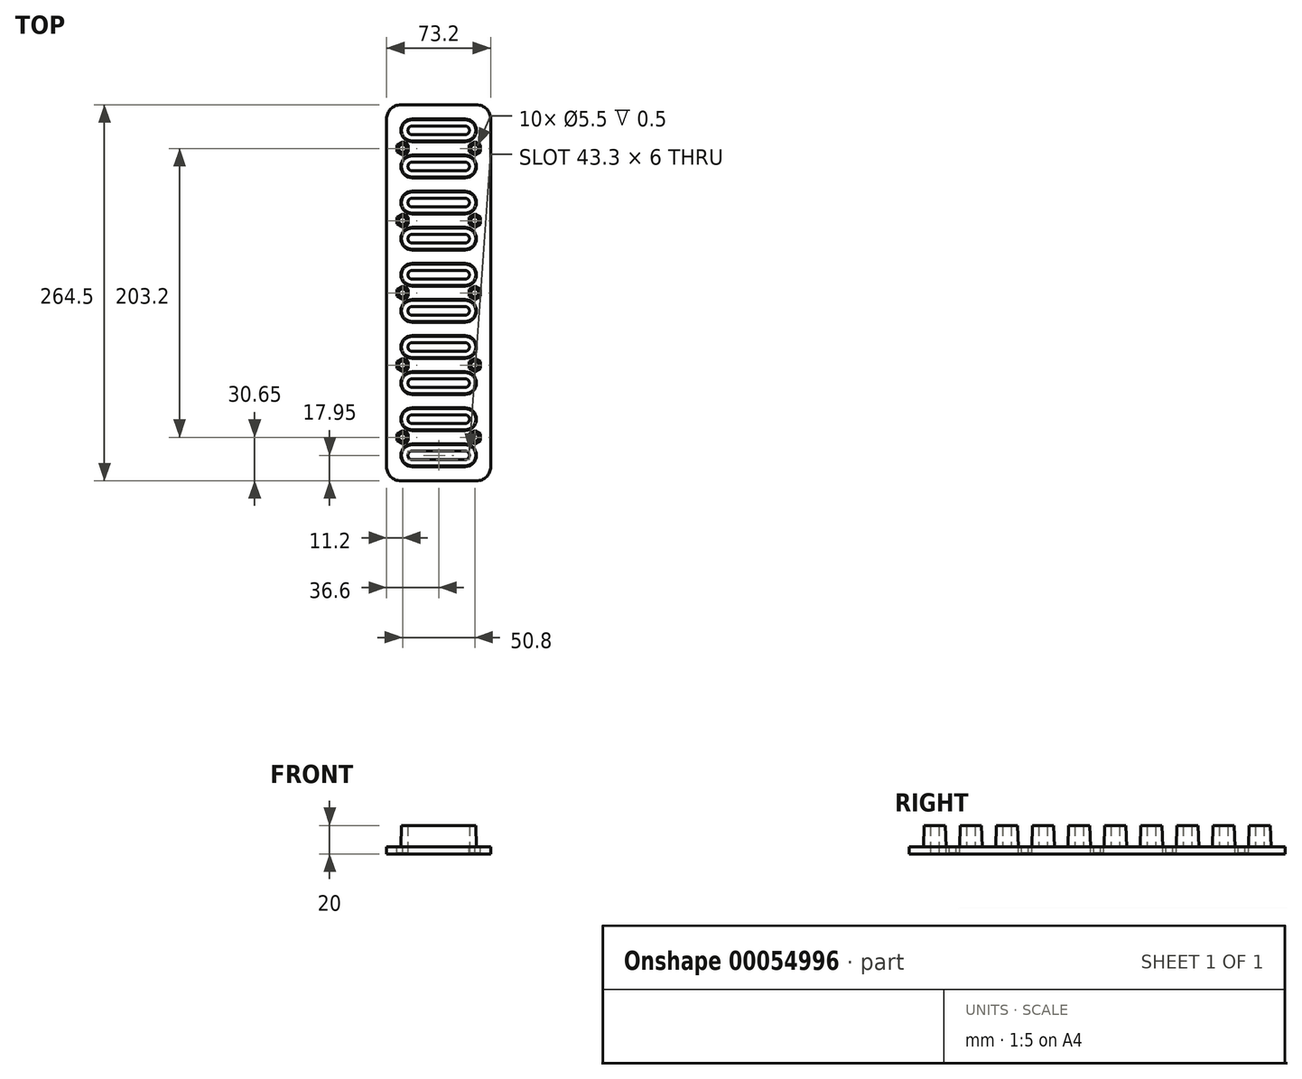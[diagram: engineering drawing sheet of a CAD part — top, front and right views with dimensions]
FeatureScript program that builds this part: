
annotation { "Feature Type Name" : "Feature", "Feature Type Description" : "" }
export const myFeature = defineFeature(function(context is Context, id is Id, definition is map)
    precondition{}
    {
        {
            var Q0;
            Q0=qCreatedBy(makeId("Top.planeOp"),FACE);
            var sketch = newSketch(context, id + "F0", { "sketchPlane" : qUnion([Q0])});
            skLineSegment(sketch, "E0.bottom", {"start": v(-18.65, 7.7) * mm, "end": v(18.65, 7.7) * mm});
            skLineSegment(sketch, "E0.top", {"start": v(-18.65, -7.7) * mm, "end": v(18.65, -7.7) * mm});
            skLineSegment(sketch, "E0.left", {"start": v(-26.35, 0) * mm, "end": v(-26.35, 0) * mm});
            skLineSegment(sketch, "E0.right", {"start": v(26.35, 0) * mm, "end": v(26.35, 0) * mm});
            skPoint(sketch, "E1", {"position": v(0, 7.7) * mm});
            skPoint(sketch, "E2", {"position": v(26.35, 0) * mm});
            skPoint(sketch, "E3.visualSharp", {"position": v(-26.35, 7.7) * mm});
            skArc(sketch, "E3.filletArc", {"start": v(-18.65, 7.7) * mm, "mid": v(-24.1, 5.44) * mm, "end": v(-26.35, 0) * mm});
            skPoint(sketch, "E4.visualSharp", {"position": v(-26.35, -7.7) * mm});
            skArc(sketch, "E4.filletArc", {"start": v(-26.35, 0) * mm, "mid": v(-24.1, -5.44) * mm, "end": v(-18.65, -7.7) * mm});
            skPoint(sketch, "E5.visualSharp", {"position": v(26.35, -7.7) * mm});
            skArc(sketch, "E5.filletArc", {"start": v(18.65, -7.7) * mm, "mid": v(24.1, -5.44) * mm, "end": v(26.35, 0) * mm});
            skPoint(sketch, "E6.visualSharp", {"position": v(26.35, 7.7) * mm});
            skArc(sketch, "E6.filletArc", {"start": v(26.35, 0) * mm, "mid": v(24.1, 5.44) * mm, "end": v(18.65, 7.7) * mm});
            skPoint(sketch, "E7.visualSharp", {"position": v(26.35, 33.1) * mm});
            skLineSegment(sketch, "E8.left", {"start": v(-26.35, 25.4) * mm, "end": v(-26.35, 25.4) * mm});
            skLineSegment(sketch, "E8.right", {"start": v(26.35, 25.4) * mm, "end": v(26.35, 25.4) * mm});
            skPoint(sketch, "E9.visualSharp", {"position": v(-26.35, 33.1) * mm});
            skLineSegment(sketch, "E8.bottom", {"start": v(-18.65, 33.1) * mm, "end": v(18.65, 33.1) * mm});
            skLineSegment(sketch, "E8.top", {"start": v(-18.65, 17.7) * mm, "end": v(18.65, 17.7) * mm});
            skArc(sketch, "E9.filletArc", {"start": v(-18.65, 33.1) * mm, "mid": v(-24.1, 30.84) * mm, "end": v(-26.35, 25.4) * mm});
            skArc(sketch, "E10.filletArc", {"start": v(-26.35, 25.4) * mm, "mid": v(-24.1, 19.96) * mm, "end": v(-18.65, 17.7) * mm});
            skArc(sketch, "E11.filletArc", {"start": v(18.65, 17.7) * mm, "mid": v(24.1, 19.96) * mm, "end": v(26.35, 25.4) * mm});
            skArc(sketch, "E7.filletArc", {"start": v(26.35, 25.4) * mm, "mid": v(24.1, 30.84) * mm, "end": v(18.65, 33.1) * mm});
            skPoint(sketch, "E10.visualSharp", {"position": v(-26.35, 17.7) * mm});
            skPoint(sketch, "E12", {"position": v(0, 33.1) * mm});
            skPoint(sketch, "E11.visualSharp", {"position": v(26.35, 17.7) * mm});
            skPoint(sketch, "E13", {"position": v(26.35, 25.4) * mm});
            skLineSegment(sketch, "E14", {"start": v(-26.35, -7.7) * mm, "end": v(-26.35, 17.7) * mm, "construction": true});
            skLineSegment(sketch, "E15.right", {"start": v(26.35, 50.8) * mm, "end": v(26.35, 50.8) * mm});
            skArc(sketch, "E16.filletArc", {"start": v(26.35, 76.2) * mm, "mid": v(24.1, 81.64) * mm, "end": v(18.65, 83.9) * mm});
            skPoint(sketch, "E17.visualSharp", {"position": v(26.35, 68.5) * mm});
            skPoint(sketch, "E18.visualSharp", {"position": v(-26.35, 58.5) * mm});
            skPoint(sketch, "E19.visualSharp", {"position": v(26.35, 58.5) * mm});
            skArc(sketch, "E20.filletArc", {"start": v(18.65, 43.1) * mm, "mid": v(24.1, 45.36) * mm, "end": v(26.35, 50.8) * mm});
            skArc(sketch, "E21.filletArc", {"start": v(-26.35, 50.8) * mm, "mid": v(-24.1, 45.36) * mm, "end": v(-18.65, 43.1) * mm});
            skLineSegment(sketch, "E15.top", {"start": v(-18.65, 43.1) * mm, "end": v(18.65, 43.1) * mm});
            skLineSegment(sketch, "E22.right", {"start": v(26.35, 76.2) * mm, "end": v(26.35, 76.2) * mm});
            skPoint(sketch, "E21.visualSharp", {"position": v(-26.35, 43.1) * mm});
            skLineSegment(sketch, "E15.left", {"start": v(-26.35, 50.8) * mm, "end": v(-26.35, 50.8) * mm});
            skPoint(sketch, "E16.visualSharp", {"position": v(26.35, 83.9) * mm});
            skPoint(sketch, "E23.visualSharp", {"position": v(-26.35, 83.9) * mm});
            skPoint(sketch, "E24.visualSharp", {"position": v(-26.35, 68.5) * mm});
            skPoint(sketch, "E25", {"position": v(0, 58.5) * mm});
            skPoint(sketch, "E26", {"position": v(0, 83.9) * mm});
            skLineSegment(sketch, "E15.bottom", {"start": v(-18.65, 58.5) * mm, "end": v(18.65, 58.5) * mm});
            skArc(sketch, "E18.filletArc", {"start": v(-18.65, 58.5) * mm, "mid": v(-24.1, 56.24) * mm, "end": v(-26.35, 50.8) * mm});
            skArc(sketch, "E19.filletArc", {"start": v(26.35, 50.8) * mm, "mid": v(24.1, 56.24) * mm, "end": v(18.65, 58.5) * mm});
            skLineSegment(sketch, "E22.left", {"start": v(-26.35, 76.2) * mm, "end": v(-26.35, 76.2) * mm});
            skPoint(sketch, "E20.visualSharp", {"position": v(26.35, 43.1) * mm});
            skLineSegment(sketch, "E22.bottom", {"start": v(-18.65, 83.9) * mm, "end": v(18.65, 83.9) * mm});
            skLineSegment(sketch, "E22.top", {"start": v(-18.65, 68.5) * mm, "end": v(18.65, 68.5) * mm});
            skArc(sketch, "E23.filletArc", {"start": v(-18.65, 83.9) * mm, "mid": v(-24.1, 81.64) * mm, "end": v(-26.35, 76.2) * mm});
            skArc(sketch, "E24.filletArc", {"start": v(-26.35, 76.2) * mm, "mid": v(-24.1, 70.76) * mm, "end": v(-18.65, 68.5) * mm});
            skArc(sketch, "E17.filletArc", {"start": v(18.65, 68.5) * mm, "mid": v(24.1, 70.76) * mm, "end": v(26.35, 76.2) * mm});
            skLineSegment(sketch, "E27", {"start": v(-26.35, 43.1) * mm, "end": v(-26.35, 68.5) * mm, "construction": true});
            skPoint(sketch, "E28", {"position": v(26.35, 76.2) * mm});
            skPoint(sketch, "E29", {"position": v(26.35, 50.8) * mm});
            skLineSegment(sketch, "E30", {"start": v(-26.35, 17.7) * mm, "end": v(-26.35, 43.1) * mm, "construction": true});
            skLineSegment(sketch, "E31.top", {"start": v(-18.65, 119.3) * mm, "end": v(18.65, 119.3) * mm});
            skArc(sketch, "E32.filletArc", {"start": v(-18.65, 109.3) * mm, "mid": v(-24.1, 107.04) * mm, "end": v(-26.35, 101.6) * mm});
            skPoint(sketch, "E33.visualSharp", {"position": v(26.35, 119.3) * mm});
            skPoint(sketch, "E32.visualSharp", {"position": v(-26.35, 109.3) * mm});
            skLineSegment(sketch, "E31.right", {"start": v(26.35, 127) * mm, "end": v(26.35, 127) * mm});
            skLineSegment(sketch, "E34", {"start": v(-26.35, 144.7) * mm, "end": v(-26.35, 170.1) * mm, "construction": true});
            skPoint(sketch, "E35.visualSharp", {"position": v(-26.35, 144.7) * mm});
            skArc(sketch, "E36.filletArc", {"start": v(-26.35, 177.8) * mm, "mid": v(-24.1, 172.36) * mm, "end": v(-18.65, 170.1) * mm});
            skLineSegment(sketch, "E37.right", {"start": v(26.35, 177.8) * mm, "end": v(26.35, 177.8) * mm});
            skLineSegment(sketch, "E31.left", {"start": v(-26.35, 127) * mm, "end": v(-26.35, 127) * mm});
            skLineSegment(sketch, "E38", {"start": v(-26.35, 93.9) * mm, "end": v(-26.35, 119.3) * mm, "construction": true});
            skArc(sketch, "E39.filletArc", {"start": v(26.35, 127) * mm, "mid": v(24.1, 132.44) * mm, "end": v(18.65, 134.7) * mm});
            skArc(sketch, "E33.filletArc", {"start": v(18.65, 119.3) * mm, "mid": v(24.1, 121.56) * mm, "end": v(26.35, 127) * mm});
            skPoint(sketch, "E40.visualSharp", {"position": v(26.35, 144.7) * mm});
            skArc(sketch, "E41.filletArc", {"start": v(-26.35, 127) * mm, "mid": v(-24.1, 121.56) * mm, "end": v(-18.65, 119.3) * mm});
            skArc(sketch, "E42.filletArc", {"start": v(-18.65, 134.7) * mm, "mid": v(-24.1, 132.44) * mm, "end": v(-26.35, 127) * mm});
            skPoint(sketch, "E42.visualSharp", {"position": v(-26.35, 134.7) * mm});
            skArc(sketch, "E43.filletArc", {"start": v(18.65, 170.1) * mm, "mid": v(24.1, 172.36) * mm, "end": v(26.35, 177.8) * mm});
            skPoint(sketch, "E44", {"position": v(0, 134.7) * mm});
            skLineSegment(sketch, "E45.right", {"start": v(26.35, 101.6) * mm, "end": v(26.35, 101.6) * mm});
            skPoint(sketch, "E36.visualSharp", {"position": v(-26.35, 170.1) * mm});
            skLineSegment(sketch, "E46", {"start": v(-26.35, 119.3) * mm, "end": v(-26.35, 144.7) * mm, "construction": true});
            skArc(sketch, "E40.filletArc", {"start": v(18.65, 144.7) * mm, "mid": v(24.1, 146.96) * mm, "end": v(26.35, 152.4) * mm});
            skLineSegment(sketch, "E47.left", {"start": v(-26.35, 152.4) * mm, "end": v(-26.35, 152.4) * mm});
            skArc(sketch, "E35.filletArc", {"start": v(-26.35, 152.4) * mm, "mid": v(-24.1, 146.96) * mm, "end": v(-18.65, 144.7) * mm});
            skLineSegment(sketch, "E45.bottom", {"start": v(-18.65, 109.3) * mm, "end": v(18.65, 109.3) * mm});
            skLineSegment(sketch, "E45.top", {"start": v(-18.65, 93.9) * mm, "end": v(18.65, 93.9) * mm});
            skArc(sketch, "E48.filletArc", {"start": v(18.65, 93.9) * mm, "mid": v(24.1, 96.16) * mm, "end": v(26.35, 101.6) * mm});
            skArc(sketch, "E49.filletArc", {"start": v(26.35, 101.6) * mm, "mid": v(24.1, 107.04) * mm, "end": v(18.65, 109.3) * mm});
            skLineSegment(sketch, "E37.left", {"start": v(-26.35, 177.8) * mm, "end": v(-26.35, 177.8) * mm});
            skPoint(sketch, "E43.visualSharp", {"position": v(26.35, 170.1) * mm});
            skLineSegment(sketch, "E37.bottom", {"start": v(-18.65, 185.5) * mm, "end": v(18.65, 185.5) * mm});
            skArc(sketch, "E50.filletArc", {"start": v(-26.35, 101.6) * mm, "mid": v(-24.1, 96.16) * mm, "end": v(-18.65, 93.9) * mm});
            skPoint(sketch, "E51", {"position": v(0, 160.1) * mm});
            skPoint(sketch, "E50.visualSharp", {"position": v(-26.35, 93.9) * mm});
            skArc(sketch, "E52.filletArc", {"start": v(26.35, 177.8) * mm, "mid": v(24.1, 183.24) * mm, "end": v(18.65, 185.5) * mm});
            skArc(sketch, "E53.filletArc", {"start": v(-18.65, 160.1) * mm, "mid": v(-24.1, 157.84) * mm, "end": v(-26.35, 152.4) * mm});
            skPoint(sketch, "E54.visualSharp", {"position": v(-26.35, 185.5) * mm});
            skLineSegment(sketch, "E47.right", {"start": v(26.35, 152.4) * mm, "end": v(26.35, 152.4) * mm});
            skLineSegment(sketch, "E47.bottom", {"start": v(-18.65, 160.1) * mm, "end": v(18.65, 160.1) * mm});
            skPoint(sketch, "E52.visualSharp", {"position": v(26.35, 185.5) * mm});
            skLineSegment(sketch, "E47.top", {"start": v(-18.65, 144.7) * mm, "end": v(18.65, 144.7) * mm});
            skArc(sketch, "E54.filletArc", {"start": v(-18.65, 185.5) * mm, "mid": v(-24.1, 183.24) * mm, "end": v(-26.35, 177.8) * mm});
            skPoint(sketch, "E55", {"position": v(0, 109.3) * mm});
            skLineSegment(sketch, "E37.top", {"start": v(-18.65, 170.1) * mm, "end": v(18.65, 170.1) * mm});
            skPoint(sketch, "E41.visualSharp", {"position": v(-26.35, 119.3) * mm});
            skPoint(sketch, "E56", {"position": v(0, 185.5) * mm});
            skLineSegment(sketch, "E45.left", {"start": v(-26.35, 101.6) * mm, "end": v(-26.35, 101.6) * mm});
            skPoint(sketch, "E49.visualSharp", {"position": v(26.35, 109.3) * mm});
            skPoint(sketch, "E57.visualSharp", {"position": v(26.35, 160.1) * mm});
            skLineSegment(sketch, "E31.bottom", {"start": v(-18.65, 134.7) * mm, "end": v(18.65, 134.7) * mm});
            skArc(sketch, "E57.filletArc", {"start": v(26.35, 152.4) * mm, "mid": v(24.1, 157.84) * mm, "end": v(18.65, 160.1) * mm});
            skPoint(sketch, "E39.visualSharp", {"position": v(26.35, 134.7) * mm});
            skPoint(sketch, "E48.visualSharp", {"position": v(26.35, 93.9) * mm});
            skPoint(sketch, "E53.visualSharp", {"position": v(-26.35, 160.1) * mm});
            skPoint(sketch, "E58", {"position": v(26.35, 152.4) * mm});
            skPoint(sketch, "E59", {"position": v(26.35, 127) * mm});
            skPoint(sketch, "E60", {"position": v(26.35, 101.6) * mm});
            skPoint(sketch, "E61", {"position": v(26.35, 177.8) * mm});
            skLineSegment(sketch, "E62", {"start": v(-26.35, 68.5) * mm, "end": v(-26.35, 93.9) * mm, "construction": true});
            skLineSegment(sketch, "E63", {"start": v(-26.35, 195.5) * mm, "end": v(-26.35, 220.9) * mm, "construction": true});
            skLineSegment(sketch, "E64.left", {"start": v(-26.35, 228.6) * mm, "end": v(-26.35, 228.6) * mm});
            skLineSegment(sketch, "E64.top", {"start": v(-18.65, 220.9) * mm, "end": v(18.65, 220.9) * mm});
            skPoint(sketch, "E65.visualSharp", {"position": v(26.35, 220.9) * mm});
            skArc(sketch, "E66.filletArc", {"start": v(-18.65, 210.9) * mm, "mid": v(-24.1, 208.64) * mm, "end": v(-26.35, 203.2) * mm});
            skPoint(sketch, "E67.visualSharp", {"position": v(-26.35, 195.5) * mm});
            skArc(sketch, "E68.filletArc", {"start": v(-18.65, 236.3) * mm, "mid": v(-24.1, 234.04) * mm, "end": v(-26.35, 228.6) * mm});
            skLineSegment(sketch, "E69", {"start": v(-26.35, 170.1) * mm, "end": v(-26.35, 195.5) * mm, "construction": true});
            skLineSegment(sketch, "E70.bottom", {"start": v(-18.65, 210.9) * mm, "end": v(18.65, 210.9) * mm});
            skPoint(sketch, "E71.visualSharp", {"position": v(26.35, 195.5) * mm});
            skLineSegment(sketch, "E70.left", {"start": v(-26.35, 203.2) * mm, "end": v(-26.35, 203.2) * mm});
            skLineSegment(sketch, "E64.bottom", {"start": v(-18.65, 236.3) * mm, "end": v(18.65, 236.3) * mm});
            skArc(sketch, "E72.filletArc", {"start": v(26.35, 203.2) * mm, "mid": v(24.1, 208.64) * mm, "end": v(18.65, 210.9) * mm});
            skArc(sketch, "E73.filletArc", {"start": v(26.35, 228.6) * mm, "mid": v(24.1, 234.04) * mm, "end": v(18.65, 236.3) * mm});
            skPoint(sketch, "E74.visualSharp", {"position": v(-26.35, 220.9) * mm});
            skArc(sketch, "E74.filletArc", {"start": v(-26.35, 228.6) * mm, "mid": v(-24.1, 223.16) * mm, "end": v(-18.65, 220.9) * mm});
            skPoint(sketch, "E66.visualSharp", {"position": v(-26.35, 210.9) * mm});
            skArc(sketch, "E65.filletArc", {"start": v(18.65, 220.9) * mm, "mid": v(24.1, 223.16) * mm, "end": v(26.35, 228.6) * mm});
            skPoint(sketch, "E72.visualSharp", {"position": v(26.35, 210.9) * mm});
            skPoint(sketch, "E75", {"position": v(0, 236.3) * mm});
            skPoint(sketch, "E68.visualSharp", {"position": v(-26.35, 236.3) * mm});
            skArc(sketch, "E67.filletArc", {"start": v(-26.35, 203.2) * mm, "mid": v(-24.1, 197.76) * mm, "end": v(-18.65, 195.5) * mm});
            skLineSegment(sketch, "E70.right", {"start": v(26.35, 203.2) * mm, "end": v(26.35, 203.2) * mm});
            skLineSegment(sketch, "E70.top", {"start": v(-18.65, 195.5) * mm, "end": v(18.65, 195.5) * mm});
            skArc(sketch, "E71.filletArc", {"start": v(18.65, 195.5) * mm, "mid": v(24.1, 197.76) * mm, "end": v(26.35, 203.2) * mm});
            skPoint(sketch, "E76", {"position": v(0, 210.9) * mm});
            skPoint(sketch, "E73.visualSharp", {"position": v(26.35, 236.3) * mm});
            skLineSegment(sketch, "E64.right", {"start": v(26.35, 228.6) * mm, "end": v(26.35, 228.6) * mm});
            skPoint(sketch, "E77", {"position": v(26.35, 203.2) * mm});
            skPoint(sketch, "E78", {"position": v(26.35, 228.6) * mm});
            skSolve(sketch);
        }
        {
            var Q0;
            Q0=qCreatedBy(makeId("Top.planeOp"),FACE);
            var sketch = newSketch(context, id + "F1", { "sketchPlane" : qUnion([Q0])});
            skLineSegment(sketch, "E79.bottom", {"start": v(-18.65, 3) * mm, "end": v(18.65, 3) * mm});
            skLineSegment(sketch, "E79.top", {"start": v(-18.65, -3) * mm, "end": v(18.65, -3) * mm});
            skLineSegment(sketch, "E79.left", {"start": v(-21.65, 0) * mm, "end": v(-21.65, 0) * mm});
            skLineSegment(sketch, "E79.right", {"start": v(21.65, 0) * mm, "end": v(21.65, 0) * mm});
            skPoint(sketch, "E80", {"position": v(0, 3) * mm});
            skPoint(sketch, "E81", {"position": v(21.65, 0) * mm});
            skPoint(sketch, "E82.visualSharp", {"position": v(-21.65, 3) * mm});
            skArc(sketch, "E82.filletArc", {"start": v(-18.65, 3) * mm, "mid": v(-20.77, 2.12) * mm, "end": v(-21.65, 0) * mm});
            skPoint(sketch, "E83.visualSharp", {"position": v(-21.65, -3) * mm});
            skArc(sketch, "E83.filletArc", {"start": v(-21.65, 0) * mm, "mid": v(-20.77, -2.12) * mm, "end": v(-18.65, -3) * mm});
            skPoint(sketch, "E84.visualSharp", {"position": v(21.65, -3) * mm});
            skArc(sketch, "E84.filletArc", {"start": v(18.65, -3) * mm, "mid": v(20.77, -2.12) * mm, "end": v(21.65, 0) * mm});
            skPoint(sketch, "E85.visualSharp", {"position": v(21.65, 3) * mm});
            skArc(sketch, "E85.filletArc", {"start": v(21.65, 0) * mm, "mid": v(20.77, 2.12) * mm, "end": v(18.65, 3) * mm});
            skPoint(sketch, "E86.visualSharp", {"position": v(21.65, 28.4) * mm});
            skLineSegment(sketch, "E87.left", {"start": v(-21.65, 25.4) * mm, "end": v(-21.65, 25.4) * mm});
            skLineSegment(sketch, "E87.right", {"start": v(21.65, 25.4) * mm, "end": v(21.65, 25.4) * mm});
            skPoint(sketch, "E88.visualSharp", {"position": v(-21.65, 22.4) * mm});
            skPoint(sketch, "E89.visualSharp", {"position": v(-21.65, 28.4) * mm});
            skLineSegment(sketch, "E87.bottom", {"start": v(-18.65, 28.4) * mm, "end": v(18.65, 28.4) * mm});
            skLineSegment(sketch, "E87.top", {"start": v(-18.65, 22.4) * mm, "end": v(18.65, 22.4) * mm});
            skPoint(sketch, "E90", {"position": v(0, 28.4) * mm});
            skPoint(sketch, "E91.visualSharp", {"position": v(21.65, 22.4) * mm});
            skPoint(sketch, "E92", {"position": v(21.65, 25.4) * mm});
            skArc(sketch, "E89.filletArc", {"start": v(-18.65, 28.4) * mm, "mid": v(-20.77, 27.52) * mm, "end": v(-21.65, 25.4) * mm});
            skArc(sketch, "E88.filletArc", {"start": v(-21.65, 25.4) * mm, "mid": v(-20.77, 23.28) * mm, "end": v(-18.65, 22.4) * mm});
            skArc(sketch, "E91.filletArc", {"start": v(18.65, 22.4) * mm, "mid": v(20.77, 23.28) * mm, "end": v(21.65, 25.4) * mm});
            skArc(sketch, "E86.filletArc", {"start": v(21.65, 25.4) * mm, "mid": v(20.77, 27.52) * mm, "end": v(18.65, 28.4) * mm});
            skLineSegment(sketch, "E93", {"start": v(-21.65, 22.4) * mm, "end": v(-21.65, -3) * mm, "construction": true});
            skLineSegment(sketch, "E94.right", {"start": v(21.65, 76.2) * mm, "end": v(21.65, 76.2) * mm});
            skPoint(sketch, "E95.visualSharp", {"position": v(-21.65, 79.2) * mm});
            skPoint(sketch, "E96.visualSharp", {"position": v(21.65, 73.2) * mm});
            skLineSegment(sketch, "E94.left", {"start": v(-21.65, 76.2) * mm, "end": v(-21.65, 76.2) * mm});
            skLineSegment(sketch, "E94.top", {"start": v(-18.65, 73.2) * mm, "end": v(18.65, 73.2) * mm});
            skLineSegment(sketch, "E94.bottom", {"start": v(-18.65, 79.2) * mm, "end": v(18.65, 79.2) * mm});
            skLineSegment(sketch, "E97.right", {"start": v(21.65, 50.8) * mm, "end": v(21.65, 50.8) * mm});
            skPoint(sketch, "E98.visualSharp", {"position": v(-21.65, 53.8) * mm});
            skPoint(sketch, "E99.visualSharp", {"position": v(21.65, 47.8) * mm});
            skPoint(sketch, "E100", {"position": v(0, 53.8) * mm});
            skPoint(sketch, "E101", {"position": v(0, 79.2) * mm});
            skLineSegment(sketch, "E102", {"start": v(-21.65, 73.2) * mm, "end": v(-21.65, 47.8) * mm, "construction": true});
            skPoint(sketch, "E103.visualSharp", {"position": v(-21.65, 73.2) * mm});
            skPoint(sketch, "E104.visualSharp", {"position": v(-21.65, 47.8) * mm});
            skPoint(sketch, "E105.visualSharp", {"position": v(21.65, 79.2) * mm});
            skLineSegment(sketch, "E97.left", {"start": v(-21.65, 50.8) * mm, "end": v(-21.65, 50.8) * mm});
            skPoint(sketch, "E106.visualSharp", {"position": v(21.65, 53.8) * mm});
            skLineSegment(sketch, "E97.top", {"start": v(-18.65, 47.8) * mm, "end": v(18.65, 47.8) * mm});
            skLineSegment(sketch, "E97.bottom", {"start": v(-18.65, 53.8) * mm, "end": v(18.65, 53.8) * mm});
            skArc(sketch, "E105.filletArc", {"start": v(21.65, 76.2) * mm, "mid": v(20.77, 78.32) * mm, "end": v(18.65, 79.2) * mm});
            skArc(sketch, "E106.filletArc", {"start": v(21.65, 50.8) * mm, "mid": v(20.77, 52.92) * mm, "end": v(18.65, 53.8) * mm});
            skArc(sketch, "E99.filletArc", {"start": v(18.65, 47.8) * mm, "mid": v(20.77, 48.68) * mm, "end": v(21.65, 50.8) * mm});
            skArc(sketch, "E95.filletArc", {"start": v(-18.65, 79.2) * mm, "mid": v(-20.77, 78.32) * mm, "end": v(-21.65, 76.2) * mm});
            skPoint(sketch, "E107", {"position": v(21.65, 76.2) * mm});
            skArc(sketch, "E96.filletArc", {"start": v(18.65, 73.2) * mm, "mid": v(20.77, 74.08) * mm, "end": v(21.65, 76.2) * mm});
            skPoint(sketch, "E108", {"position": v(21.65, 50.8) * mm});
            skArc(sketch, "E98.filletArc", {"start": v(-18.65, 53.8) * mm, "mid": v(-20.77, 52.92) * mm, "end": v(-21.65, 50.8) * mm});
            skArc(sketch, "E103.filletArc", {"start": v(-21.65, 76.2) * mm, "mid": v(-20.77, 74.08) * mm, "end": v(-18.65, 73.2) * mm});
            skArc(sketch, "E104.filletArc", {"start": v(-21.65, 50.8) * mm, "mid": v(-20.77, 48.68) * mm, "end": v(-18.65, 47.8) * mm});
            skLineSegment(sketch, "E109", {"start": v(-21.65, 22.4) * mm, "end": v(-21.65, 47.8) * mm, "construction": true});
            skPoint(sketch, "E110.visualSharp", {"position": v(-21.65, 130) * mm});
            skPoint(sketch, "E111.visualSharp", {"position": v(21.65, 180.8) * mm});
            skLineSegment(sketch, "E112.right", {"start": v(21.65, 177.8) * mm, "end": v(21.65, 177.8) * mm});
            skPoint(sketch, "E113.visualSharp", {"position": v(-21.65, 155.4) * mm});
            skLineSegment(sketch, "E112.left", {"start": v(-21.65, 177.8) * mm, "end": v(-21.65, 177.8) * mm});
            skPoint(sketch, "E114.visualSharp", {"position": v(21.65, 155.4) * mm});
            skPoint(sketch, "E115", {"position": v(0, 130) * mm});
            skLineSegment(sketch, "E116", {"start": v(-21.65, 124) * mm, "end": v(-21.65, 149.4) * mm, "construction": true});
            skLineSegment(sketch, "E117.top", {"start": v(-18.65, 124) * mm, "end": v(18.65, 124) * mm});
            skPoint(sketch, "E118.visualSharp", {"position": v(-21.65, 98.6) * mm});
            skLineSegment(sketch, "E119.left", {"start": v(-21.65, 101.6) * mm, "end": v(-21.65, 101.6) * mm});
            skLineSegment(sketch, "E120.left", {"start": v(-21.65, 152.4) * mm, "end": v(-21.65, 152.4) * mm});
            skPoint(sketch, "E121.visualSharp", {"position": v(21.65, 149.4) * mm});
            skLineSegment(sketch, "E119.right", {"start": v(21.65, 101.6) * mm, "end": v(21.65, 101.6) * mm});
            skPoint(sketch, "E122.visualSharp", {"position": v(-21.65, 180.8) * mm});
            skPoint(sketch, "E123", {"position": v(0, 104.6) * mm});
            skLineSegment(sketch, "E117.left", {"start": v(-21.65, 127) * mm, "end": v(-21.65, 127) * mm});
            skPoint(sketch, "E124.visualSharp", {"position": v(-21.65, 174.8) * mm});
            skLineSegment(sketch, "E120.top", {"start": v(-18.65, 149.4) * mm, "end": v(18.65, 149.4) * mm});
            skPoint(sketch, "E125", {"position": v(0, 180.8) * mm});
            skLineSegment(sketch, "E120.right", {"start": v(21.65, 152.4) * mm, "end": v(21.65, 152.4) * mm});
            skPoint(sketch, "E126", {"position": v(0, 155.4) * mm});
            skPoint(sketch, "E127.visualSharp", {"position": v(21.65, 98.6) * mm});
            skPoint(sketch, "E128.visualSharp", {"position": v(21.65, 104.6) * mm});
            skPoint(sketch, "E129.visualSharp", {"position": v(21.65, 124) * mm});
            skPoint(sketch, "E130.visualSharp", {"position": v(-21.65, 104.6) * mm});
            skLineSegment(sketch, "E120.bottom", {"start": v(-18.65, 155.4) * mm, "end": v(18.65, 155.4) * mm});
            skLineSegment(sketch, "E131", {"start": v(-21.65, 124) * mm, "end": v(-21.65, 98.6) * mm, "construction": true});
            skLineSegment(sketch, "E117.bottom", {"start": v(-18.65, 130) * mm, "end": v(18.65, 130) * mm});
            skLineSegment(sketch, "E119.top", {"start": v(-18.65, 98.6) * mm, "end": v(18.65, 98.6) * mm});
            skLineSegment(sketch, "E119.bottom", {"start": v(-18.65, 104.6) * mm, "end": v(18.65, 104.6) * mm});
            skLineSegment(sketch, "E132", {"start": v(-21.65, 174.8) * mm, "end": v(-21.65, 149.4) * mm, "construction": true});
            skLineSegment(sketch, "E112.bottom", {"start": v(-18.65, 180.8) * mm, "end": v(18.65, 180.8) * mm});
            skLineSegment(sketch, "E112.top", {"start": v(-18.65, 174.8) * mm, "end": v(18.65, 174.8) * mm});
            skPoint(sketch, "E133.visualSharp", {"position": v(-21.65, 124) * mm});
            skPoint(sketch, "E134.visualSharp", {"position": v(-21.65, 149.4) * mm});
            skLineSegment(sketch, "E117.right", {"start": v(21.65, 127) * mm, "end": v(21.65, 127) * mm});
            skPoint(sketch, "E135.visualSharp", {"position": v(21.65, 174.8) * mm});
            skPoint(sketch, "E136.visualSharp", {"position": v(21.65, 130) * mm});
            skPoint(sketch, "E137", {"position": v(21.65, 177.8) * mm});
            skArc(sketch, "E136.filletArc", {"start": v(21.65, 127) * mm, "mid": v(20.77, 129.12) * mm, "end": v(18.65, 130) * mm});
            skArc(sketch, "E129.filletArc", {"start": v(18.65, 124) * mm, "mid": v(20.77, 124.88) * mm, "end": v(21.65, 127) * mm});
            skArc(sketch, "E114.filletArc", {"start": v(21.65, 152.4) * mm, "mid": v(20.77, 154.52) * mm, "end": v(18.65, 155.4) * mm});
            skArc(sketch, "E122.filletArc", {"start": v(-18.65, 180.8) * mm, "mid": v(-20.77, 179.92) * mm, "end": v(-21.65, 177.8) * mm});
            skArc(sketch, "E135.filletArc", {"start": v(18.65, 174.8) * mm, "mid": v(20.77, 175.68) * mm, "end": v(21.65, 177.8) * mm});
            skArc(sketch, "E111.filletArc", {"start": v(21.65, 177.8) * mm, "mid": v(20.77, 179.92) * mm, "end": v(18.65, 180.8) * mm});
            skPoint(sketch, "E138", {"position": v(21.65, 152.4) * mm});
            skArc(sketch, "E110.filletArc", {"start": v(-18.65, 130) * mm, "mid": v(-20.77, 129.12) * mm, "end": v(-21.65, 127) * mm});
            skPoint(sketch, "E139", {"position": v(21.65, 127) * mm});
            skPoint(sketch, "E140", {"position": v(21.65, 101.6) * mm});
            skArc(sketch, "E134.filletArc", {"start": v(-21.65, 152.4) * mm, "mid": v(-20.77, 150.28) * mm, "end": v(-18.65, 149.4) * mm});
            skArc(sketch, "E121.filletArc", {"start": v(18.65, 149.4) * mm, "mid": v(20.77, 150.28) * mm, "end": v(21.65, 152.4) * mm});
            skArc(sketch, "E127.filletArc", {"start": v(18.65, 98.6) * mm, "mid": v(20.77, 99.48) * mm, "end": v(21.65, 101.6) * mm});
            skArc(sketch, "E128.filletArc", {"start": v(21.65, 101.6) * mm, "mid": v(20.77, 103.72) * mm, "end": v(18.65, 104.6) * mm});
            skArc(sketch, "E130.filletArc", {"start": v(-18.65, 104.6) * mm, "mid": v(-20.77, 103.72) * mm, "end": v(-21.65, 101.6) * mm});
            skArc(sketch, "E113.filletArc", {"start": v(-18.65, 155.4) * mm, "mid": v(-20.77, 154.52) * mm, "end": v(-21.65, 152.4) * mm});
            skArc(sketch, "E133.filletArc", {"start": v(-21.65, 127) * mm, "mid": v(-20.77, 124.88) * mm, "end": v(-18.65, 124) * mm});
            skArc(sketch, "E124.filletArc", {"start": v(-21.65, 177.8) * mm, "mid": v(-20.77, 175.68) * mm, "end": v(-18.65, 174.8) * mm});
            skArc(sketch, "E118.filletArc", {"start": v(-21.65, 101.6) * mm, "mid": v(-20.77, 99.48) * mm, "end": v(-18.65, 98.6) * mm});
            skLineSegment(sketch, "E141", {"start": v(-21.65, 98.6) * mm, "end": v(-21.65, 73.2) * mm, "construction": true});
            skLineSegment(sketch, "E142.right", {"start": v(21.65, 228.6) * mm, "end": v(21.65, 228.6) * mm});
            skLineSegment(sketch, "E142.left", {"start": v(-21.65, 228.6) * mm, "end": v(-21.65, 228.6) * mm});
            skPoint(sketch, "E143.visualSharp", {"position": v(-21.65, 200.2) * mm});
            skPoint(sketch, "E144.visualSharp", {"position": v(21.65, 231.6) * mm});
            skPoint(sketch, "E145.visualSharp", {"position": v(21.65, 206.2) * mm});
            skPoint(sketch, "E146.visualSharp", {"position": v(21.65, 225.6) * mm});
            skPoint(sketch, "E147.visualSharp", {"position": v(-21.65, 206.2) * mm});
            skPoint(sketch, "E148", {"position": v(0, 206.2) * mm});
            skLineSegment(sketch, "E149", {"start": v(-21.65, 225.6) * mm, "end": v(-21.65, 200.2) * mm, "construction": true});
            skPoint(sketch, "E150.visualSharp", {"position": v(21.65, 200.2) * mm});
            skLineSegment(sketch, "E151.right", {"start": v(21.65, 203.2) * mm, "end": v(21.65, 203.2) * mm});
            skLineSegment(sketch, "E142.top", {"start": v(-18.65, 225.6) * mm, "end": v(18.65, 225.6) * mm});
            skLineSegment(sketch, "E152", {"start": v(-21.65, 174.8) * mm, "end": v(-21.65, 200.2) * mm, "construction": true});
            skPoint(sketch, "E153.visualSharp", {"position": v(-21.65, 231.6) * mm});
            skLineSegment(sketch, "E151.top", {"start": v(-18.65, 200.2) * mm, "end": v(18.65, 200.2) * mm});
            skPoint(sketch, "E154.visualSharp", {"position": v(-21.65, 225.6) * mm});
            skPoint(sketch, "E155", {"position": v(0, 231.6) * mm});
            skLineSegment(sketch, "E151.bottom", {"start": v(-18.65, 206.2) * mm, "end": v(18.65, 206.2) * mm});
            skLineSegment(sketch, "E142.bottom", {"start": v(-18.65, 231.6) * mm, "end": v(18.65, 231.6) * mm});
            skLineSegment(sketch, "E151.left", {"start": v(-21.65, 203.2) * mm, "end": v(-21.65, 203.2) * mm});
            skPoint(sketch, "E156", {"position": v(21.65, 228.6) * mm});
            skPoint(sketch, "E157", {"position": v(21.65, 203.2) * mm});
            skArc(sketch, "E150.filletArc", {"start": v(18.65, 200.2) * mm, "mid": v(20.77, 201.08) * mm, "end": v(21.65, 203.2) * mm});
            skArc(sketch, "E143.filletArc", {"start": v(-21.65, 203.2) * mm, "mid": v(-20.77, 201.08) * mm, "end": v(-18.65, 200.2) * mm});
            skArc(sketch, "E154.filletArc", {"start": v(-21.65, 228.6) * mm, "mid": v(-20.77, 226.48) * mm, "end": v(-18.65, 225.6) * mm});
            skArc(sketch, "E144.filletArc", {"start": v(21.65, 228.6) * mm, "mid": v(20.77, 230.72) * mm, "end": v(18.65, 231.6) * mm});
            skArc(sketch, "E146.filletArc", {"start": v(18.65, 225.6) * mm, "mid": v(20.77, 226.48) * mm, "end": v(21.65, 228.6) * mm});
            skArc(sketch, "E147.filletArc", {"start": v(-18.65, 206.2) * mm, "mid": v(-20.77, 205.32) * mm, "end": v(-21.65, 203.2) * mm});
            skArc(sketch, "E145.filletArc", {"start": v(21.65, 203.2) * mm, "mid": v(20.77, 205.32) * mm, "end": v(18.65, 206.2) * mm});
            skArc(sketch, "E153.filletArc", {"start": v(-18.65, 231.6) * mm, "mid": v(-20.77, 230.72) * mm, "end": v(-21.65, 228.6) * mm});
            skSolve(sketch);
        }
        {
            var Q0;
            Q0=makeQuery(id+"F0.imprint","IMPRINT",FACE,{"disambiguationData":[TD([[makeQuery(id+"F0.imprint","IMPRINT",EDGE,{"derivedFrom":sQuery(id+"F0.wireOp",EDGE,"E0.bottom")}),-1.0]])]});
            var Q1;
            Q1=makeQuery(id+"F0.imprint","IMPRINT",FACE,{"disambiguationData":[TD([[makeQuery(id+"F0.imprint","IMPRINT",EDGE,{"derivedFrom":sQuery(id+"F0.wireOp",EDGE,"E8.bottom")}),-1.0]])]});
            var Q2;
            Q2=makeQuery(id+"F0.imprint","IMPRINT",FACE,{"disambiguationData":[TD([[makeQuery(id+"F0.imprint","IMPRINT",EDGE,{"derivedFrom":sQuery(id+"F0.wireOp",EDGE,"E20.filletArc")}),1.0]])]});
            var Q3;
            Q3=makeQuery(id+"F0.imprint","IMPRINT",FACE,{"disambiguationData":[TD([[makeQuery(id+"F0.imprint","IMPRINT",EDGE,{"derivedFrom":sQuery(id+"F0.wireOp",EDGE,"E16.filletArc")}),1.0]])]});
            var Q4;
            Q4=makeQuery(id+"F0.imprint","IMPRINT",FACE,{"disambiguationData":[TD([[makeQuery(id+"F0.imprint","IMPRINT",EDGE,{"derivedFrom":sQuery(id+"F0.wireOp",EDGE,"E32.filletArc")}),1.0]])]});
            var Q5;
            Q5=makeQuery(id+"F0.imprint","IMPRINT",FACE,{"disambiguationData":[TD([[makeQuery(id+"F0.imprint","IMPRINT",EDGE,{"derivedFrom":sQuery(id+"F0.wireOp",EDGE,"E31.top")}),1.0]])]});
            var Q6;
            Q6=makeQuery(id+"F0.imprint","IMPRINT",FACE,{"disambiguationData":[TD([[makeQuery(id+"F0.imprint","IMPRINT",EDGE,{"derivedFrom":sQuery(id+"F0.wireOp",EDGE,"E40.filletArc")}),1.0]])]});
            var Q7;
            Q7=makeQuery(id+"F0.imprint","IMPRINT",FACE,{"disambiguationData":[TD([[makeQuery(id+"F0.imprint","IMPRINT",EDGE,{"derivedFrom":sQuery(id+"F0.wireOp",EDGE,"E36.filletArc")}),1.0]])]});
            var Q8;
            Q8=makeQuery(id+"F0.imprint","IMPRINT",FACE,{"disambiguationData":[TD([[makeQuery(id+"F0.imprint","IMPRINT",EDGE,{"derivedFrom":sQuery(id+"F0.wireOp",EDGE,"E66.filletArc")}),1.0]])]});
            var Q9;
            Q9=makeQuery(id+"F0.imprint","IMPRINT",FACE,{"disambiguationData":[TD([[makeQuery(id+"F0.imprint","IMPRINT",EDGE,{"derivedFrom":sQuery(id+"F0.wireOp",EDGE,"E64.top")}),1.0]])]});
            extrude(context, id + "F2", {"entities" : qUnion([Q0, Q1, Q2, Q3, Q4, Q5, Q6, Q7, Q8, Q9]), "depth" : 7.5 * mm, "hasDraft" : true, "draftAngle" : 1.9 * degree, "draftPullDirection" : true, "hasSecondDirection" : true, "secondDirectionOppositeDirection" : true, "secondDirectionDepth" : 7.5 * mm, "hasSecondDirectionDraft" : true, "secondDirectionDraftAngle" : 1.9 * degree});
        }
        {
            var Q0;
            Q0=makeQuery(id+"F1.imprint","IMPRINT",FACE,{"disambiguationData":[TD([[makeQuery(id+"F1.imprint","IMPRINT",EDGE,{"derivedFrom":sQuery(id+"F1.wireOp",EDGE,"E79.bottom")}),-1.0]])]});
            var Q1;
            Q1=makeQuery(id+"F1.imprint","IMPRINT",FACE,{"disambiguationData":[TD([[makeQuery(id+"F1.imprint","IMPRINT",EDGE,{"derivedFrom":sQuery(id+"F1.wireOp",EDGE,"E87.bottom")}),-1.0]])]});
            var Q2;
            Q2=makeQuery(id+"F1.imprint","IMPRINT",FACE,{"disambiguationData":[TD([[makeQuery(id+"F1.imprint","IMPRINT",EDGE,{"derivedFrom":sQuery(id+"F1.wireOp",EDGE,"E97.top")}),1.0]])]});
            var Q3;
            Q3=makeQuery(id+"F1.imprint","IMPRINT",FACE,{"disambiguationData":[TD([[makeQuery(id+"F1.imprint","IMPRINT",EDGE,{"derivedFrom":sQuery(id+"F1.wireOp",EDGE,"E94.top")}),1.0]])]});
            var Q4;
            Q4=makeQuery(id+"F1.imprint","IMPRINT",FACE,{"disambiguationData":[TD([[makeQuery(id+"F1.imprint","IMPRINT",EDGE,{"derivedFrom":sQuery(id+"F1.wireOp",EDGE,"E119.top")}),1.0]])]});
            var Q5;
            Q5=makeQuery(id+"F1.imprint","IMPRINT",FACE,{"disambiguationData":[TD([[makeQuery(id+"F1.imprint","IMPRINT",EDGE,{"derivedFrom":sQuery(id+"F1.wireOp",EDGE,"E117.top")}),1.0]])]});
            var Q6;
            Q6=makeQuery(id+"F1.imprint","IMPRINT",FACE,{"disambiguationData":[TD([[makeQuery(id+"F1.imprint","IMPRINT",EDGE,{"derivedFrom":sQuery(id+"F1.wireOp",EDGE,"E120.top")}),1.0]])]});
            var Q7;
            Q7=makeQuery(id+"F1.imprint","IMPRINT",FACE,{"disambiguationData":[TD([[makeQuery(id+"F1.imprint","IMPRINT",EDGE,{"derivedFrom":sQuery(id+"F1.wireOp",EDGE,"E151.top")}),1.0]])]});
            var Q8;
            Q8=makeQuery(id+"F1.imprint","IMPRINT",FACE,{"disambiguationData":[TD([[makeQuery(id+"F1.imprint","IMPRINT",EDGE,{"derivedFrom":sQuery(id+"F1.wireOp",EDGE,"E112.bottom")}),-1.0]])]});
            var Q9;
            Q9=makeQuery(id+"F1.imprint","IMPRINT",FACE,{"disambiguationData":[TD([[makeQuery(id+"F1.imprint","IMPRINT",EDGE,{"derivedFrom":sQuery(id+"F1.wireOp",EDGE,"E142.top")}),1.0]])]});
            var Q10;
            Q10=makeQuery(id+"F2.opExtrude","CAP_FACE",FACE,{"disambiguationData":[OSD([sQuery(id+"F0.wireOp",EDGE,"E0.bottom"),sQuery(id+"F0.wireOp",EDGE,"E0.top"),sQuery(id+"F0.wireOp",EDGE,"E0.left"),sQuery(id+"F0.wireOp",EDGE,"E0.right"),sQuery(id+"F0.wireOp",EDGE,"E3.filletArc"),sQuery(id+"F0.wireOp",EDGE,"E4.filletArc"),sQuery(id+"F0.wireOp",EDGE,"E5.filletArc"),sQuery(id+"F0.wireOp",EDGE,"E6.filletArc")])],"isStart":false});
            var Q11;
            Q11=makeQuery(id+"F2.opExtrude","CAP_FACE",FACE,{"disambiguationData":[OSD([sQuery(id+"F0.wireOp",EDGE,"E0.bottom"),sQuery(id+"F0.wireOp",EDGE,"E0.top"),sQuery(id+"F0.wireOp",EDGE,"E0.left"),sQuery(id+"F0.wireOp",EDGE,"E0.right"),sQuery(id+"F0.wireOp",EDGE,"E3.filletArc"),sQuery(id+"F0.wireOp",EDGE,"E4.filletArc"),sQuery(id+"F0.wireOp",EDGE,"E5.filletArc"),sQuery(id+"F0.wireOp",EDGE,"E6.filletArc")])],"isStart":true});
            extrude(context, id + "F3", {"entities" : qUnion([Q0, Q1, Q2, Q3, Q4, Q5, Q6, Q7, Q8, Q9]), "operationType" : NewBodyOperationType.REMOVE, "endBound" : BoundingType.UP_TO_SURFACE, "endBoundEntityFace" : qUnion([Q10]), "depth" : 10 * mm, "hasSecondDirection" : true, "secondDirectionBound" : SecondDirectionBoundingType.UP_TO_SURFACE, "secondDirectionOppositeDirection" : true, "secondDirectionBoundEntityFace" : qUnion([Q11]), "secondDirectionDepth" : 25 * mm});
        }
        {
            var Q0;
            Q0=makeQuery(id+"F2.opExtrude","CAP_FACE",FACE,{"disambiguationData":[OSD([sQuery(id+"F0.wireOp",EDGE,"E0.bottom"),sQuery(id+"F0.wireOp",EDGE,"E0.top"),sQuery(id+"F0.wireOp",EDGE,"E3.filletArc"),sQuery(id+"F0.wireOp",EDGE,"E4.filletArc"),sQuery(id+"F0.wireOp",EDGE,"E5.filletArc"),sQuery(id+"F0.wireOp",EDGE,"E6.filletArc")])],"isStart":true});
            var sketch = newSketch(context, id + "F4", { "sketchPlane" : qUnion([Q0])});
            skLineSegment(sketch, "E158", {"start": v(0, 0) * mm, "end": v(25.4, 0) * mm, "construction": true});
            skLineSegment(sketch, "E159", {"start": v(25.4, 0) * mm, "end": v(50.8, 0) * mm, "construction": true});
            skLineSegment(sketch, "E160", {"start": v(0, 0) * mm, "end": v(-25.4, 0) * mm, "construction": true});
            skLineSegment(sketch, "E161", {"start": v(-25.4, 0) * mm, "end": v(-50.8, 0) * mm, "construction": true});
            skLineSegment(sketch, "E162", {"start": v(0, 0) * mm, "end": v(0, 25.4) * mm, "construction": true});
            skLineSegment(sketch, "E163", {"start": v(0, 0) * mm, "end": v(0, -25.4) * mm, "construction": true});
            skLineSegment(sketch, "E164", {"start": v(0, -25.4) * mm, "end": v(0, -50.8) * mm, "construction": true});
            skLineSegment(sketch, "E165.0.0", {"start": v(-18.65, -7.95) * mm, "end": v(18.65, -7.95) * mm});
            skLineSegment(sketch, "E165.0.1", {"start": v(18.65, -7.95) * mm, "end": v(18.65, -7.95) * mm});
            skLineSegment(sketch, "E165.0.4", {"start": v(-18.65, 7.95) * mm, "end": v(18.65, 7.95) * mm});
            skLineSegment(sketch, "E165.0.5", {"start": v(-18.65, 7.95) * mm, "end": v(-18.65, 7.95) * mm});
            skLineSegment(sketch, "E166.2", {"start": v(31.6, -0.23) * mm, "end": v(31.6, -0.23) * mm});
            skLineSegment(sketch, "E166.7", {"start": v(-31.6, 0.23) * mm, "end": v(-31.6, 0.23) * mm});
            skArc(sketch, "E167.0", {"start": v(-18.65, -2.95) * mm, "mid": v(-21.6, 0) * mm, "end": v(-18.65, 2.95) * mm});
            skLineSegment(sketch, "E167.1", {"start": v(-18.65, -2.95) * mm, "end": v(18.65, -2.95) * mm});
            skArc(sketch, "E167.2", {"start": v(18.65, 2.95) * mm, "mid": v(21.6, 0) * mm, "end": v(18.65, -2.95) * mm});
            skLineSegment(sketch, "E167.3", {"start": v(-18.65, 2.95) * mm, "end": v(18.65, 2.95) * mm});
            skLineSegment(sketch, "E168.bottom", {"start": v(26.6, 17.95) * mm, "end": v(-26.6, 17.95) * mm});
            skLineSegment(sketch, "E168.top", {"start": v(26.6, -246.55) * mm, "end": v(-26.6, -246.55) * mm});
            skLineSegment(sketch, "E168.left", {"start": v(36.6, 7.95) * mm, "end": v(36.6, -236.55) * mm});
            skLineSegment(sketch, "E168.right", {"start": v(-36.6, 7.95) * mm, "end": v(-36.6, -236.55) * mm});
            skLineSegment(sketch, "E169", {"start": v(18.65, 7.95) * mm, "end": v(18.65, 17.95) * mm, "construction": true});
            skArc(sketch, "E170.0.0", {"start": v(-18.65, -220.65) * mm, "mid": v(-26.6, -228.6) * mm, "end": v(-18.65, -236.55) * mm, "construction": true});
            skLineSegment(sketch, "E170.0.1", {"start": v(-18.65, -236.55) * mm, "end": v(18.65, -236.55) * mm, "construction": true});
            skArc(sketch, "E170.0.2", {"start": v(18.65, -236.55) * mm, "mid": v(26.6, -228.6) * mm, "end": v(18.65, -220.65) * mm, "construction": true});
            skLineSegment(sketch, "E170.0.3", {"start": v(-18.65, -220.65) * mm, "end": v(18.65, -220.65) * mm, "construction": true});
            skLineSegment(sketch, "E171", {"start": v(18.65, -236.55) * mm, "end": v(18.65, -246.55) * mm, "construction": true});
            skLineSegment(sketch, "E172", {"start": v(26.6, -228.6) * mm, "end": v(36.6, -228.6) * mm, "construction": true});
            skLineSegment(sketch, "E173", {"start": v(-26.6, -228.6) * mm, "end": v(-36.6, -228.6) * mm, "construction": true});
            skPoint(sketch, "E174.visualSharp", {"position": v(36.6, 17.95) * mm});
            skArc(sketch, "E174.filletArc", {"start": v(36.6, 7.95) * mm, "mid": v(33.67, 15.02) * mm, "end": v(26.6, 17.95) * mm});
            skPoint(sketch, "E175.visualSharp", {"position": v(-36.6, 17.95) * mm});
            skArc(sketch, "E175.filletArc", {"start": v(-26.6, 17.95) * mm, "mid": v(-33.67, 15.02) * mm, "end": v(-36.6, 7.95) * mm});
            skPoint(sketch, "E176.visualSharp", {"position": v(36.6, -246.55) * mm});
            skArc(sketch, "E176.filletArc", {"start": v(26.6, -246.55) * mm, "mid": v(33.67, -243.62) * mm, "end": v(36.6, -236.55) * mm});
            skPoint(sketch, "E177.visualSharp", {"position": v(-36.6, -246.55) * mm});
            skArc(sketch, "E177.filletArc", {"start": v(-36.6, -236.55) * mm, "mid": v(-33.67, -243.62) * mm, "end": v(-26.6, -246.55) * mm});
            skLineSegment(sketch, "E178.0", {"start": v(-18.65, -109.55) * mm, "end": v(18.65, -109.55) * mm, "construction": true});
            skLineSegment(sketch, "E179.0", {"start": v(-18.65, -119.05) * mm, "end": v(18.65, -119.05) * mm, "construction": true});
            skPoint(sketch, "E180", {"position": v(0, -109.55) * mm});
            skPoint(sketch, "E181", {"position": v(0, -119.05) * mm});
            skLineSegment(sketch, "E182", {"start": v(0, -109.55) * mm, "end": v(0, -119.05) * mm, "construction": true});
            skPoint(sketch, "E183", {"position": v(0, -114.3) * mm});
            skLineSegment(sketch, "E184", {"start": v(0, -114.3) * mm, "end": v(25.4, -114.3) * mm, "construction": true});
            skPoint(sketch, "E184.endSnap0", {"position": v(36.6, -114.3) * mm});
            skLineSegment(sketch, "E185", {"start": v(0, -114.3) * mm, "end": v(-25.4, -114.3) * mm, "construction": true});
            skPoint(sketch, "E185.endSnap0", {"position": v(-36.6, -114.3) * mm});
            skLineSegment(sketch, "E186.4", {"start": v(21.3, -111.93) * mm, "end": v(25.4, -109.57) * mm});
            skLineSegment(sketch, "E186.5", {"start": v(25.4, -109.57) * mm, "end": v(29.5, -111.93) * mm});
            skLineSegment(sketch, "E186.2", {"start": v(25.4, -119.03) * mm, "end": v(21.3, -116.67) * mm});
            skCircle(sketch, "E186.cCircle", {"center": v(25.4, -114.3) * mm, "radius": 4.1 * mm, "construction": true});
            skCircle(sketch, "E187", {"center": v(25.4, -114.3) * mm, "radius": 2.75 * mm});
            skLineSegment(sketch, "E188", {"start": v(25.4, -114.3) * mm, "end": v(29.5, -114.3) * mm, "construction": true});
            skLineSegment(sketch, "E186.3", {"start": v(21.3, -116.67) * mm, "end": v(21.3, -111.93) * mm});
            skLineSegment(sketch, "E186.0", {"start": v(29.5, -111.93) * mm, "end": v(29.5, -116.67) * mm});
            skPoint(sketch, "E186.0.midPoint", {"position": v(29.5, -114.3) * mm});
            skLineSegment(sketch, "E186.1", {"start": v(29.5, -116.67) * mm, "end": v(25.4, -119.03) * mm});
            skLineSegment(sketch, "E189.4", {"start": v(-29.5, -111.93) * mm, "end": v(-25.4, -109.57) * mm});
            skLineSegment(sketch, "E189.5", {"start": v(-25.4, -109.57) * mm, "end": v(-21.3, -111.93) * mm});
            skLineSegment(sketch, "E189.2", {"start": v(-25.4, -119.03) * mm, "end": v(-29.5, -116.67) * mm});
            skCircle(sketch, "E189.cCircle", {"center": v(-25.4, -114.3) * mm, "radius": 4.1 * mm, "construction": true});
            skCircle(sketch, "E190", {"center": v(-25.4, -114.3) * mm, "radius": 2.75 * mm});
            skLineSegment(sketch, "E191", {"start": v(-25.4, -114.3) * mm, "end": v(-21.3, -114.3) * mm, "construction": true});
            skLineSegment(sketch, "E189.3", {"start": v(-29.5, -116.67) * mm, "end": v(-29.5, -111.93) * mm});
            skLineSegment(sketch, "E189.0", {"start": v(-21.3, -111.93) * mm, "end": v(-21.3, -116.67) * mm});
            skPoint(sketch, "E189.0.midPoint", {"position": v(-21.3, -114.3) * mm});
            skLineSegment(sketch, "E189.1", {"start": v(-21.3, -116.67) * mm, "end": v(-25.4, -119.03) * mm});
            skPoint(sketch, "E192", {"position": v(0, -160.35) * mm});
            skPoint(sketch, "E193.endSnap0", {"position": v(-36.6, -165.1) * mm});
            skLineSegment(sketch, "E194.1", {"start": v(29.5, -167.47) * mm, "end": v(25.4, -169.83) * mm});
            skPoint(sketch, "E195", {"position": v(0, -169.85) * mm});
            skLineSegment(sketch, "E196", {"start": v(0, -165.1) * mm, "end": v(25.4, -165.1) * mm, "construction": true});
            skLineSegment(sketch, "E193", {"start": v(0, -165.1) * mm, "end": v(-25.4, -165.1) * mm, "construction": true});
            skLineSegment(sketch, "E194.3", {"start": v(21.3, -167.47) * mm, "end": v(21.3, -162.73) * mm});
            skLineSegment(sketch, "E197.3", {"start": v(-29.5, -167.47) * mm, "end": v(-29.5, -162.73) * mm});
            skCircle(sketch, "E198", {"center": v(25.4, -165.1) * mm, "radius": 2.75 * mm});
            skLineSegment(sketch, "E199.0", {"start": v(-18.65, -160.35) * mm, "end": v(18.65, -160.35) * mm, "construction": true});
            skPoint(sketch, "E194.0.midPoint", {"position": v(29.5, -165.1) * mm});
            skPoint(sketch, "E197.0.midPoint", {"position": v(-21.3, -165.1) * mm});
            skPoint(sketch, "E200", {"position": v(0, -165.1) * mm});
            skCircle(sketch, "E201", {"center": v(-25.4, -165.1) * mm, "radius": 2.75 * mm});
            skPoint(sketch, "E196.endSnap0", {"position": v(36.6, -165.1) * mm});
            skLineSegment(sketch, "E202.0", {"start": v(-18.65, -169.85) * mm, "end": v(18.65, -169.85) * mm, "construction": true});
            skLineSegment(sketch, "E203", {"start": v(25.4, -165.1) * mm, "end": v(29.5, -165.1) * mm, "construction": true});
            skLineSegment(sketch, "E194.4", {"start": v(21.3, -162.73) * mm, "end": v(25.4, -160.37) * mm});
            skCircle(sketch, "E194.cCircle", {"center": v(25.4, -165.1) * mm, "radius": 4.1 * mm, "construction": true});
            skCircle(sketch, "E197.cCircle", {"center": v(-25.4, -165.1) * mm, "radius": 4.1 * mm, "construction": true});
            skLineSegment(sketch, "E204", {"start": v(0, -160.35) * mm, "end": v(0, -169.85) * mm, "construction": true});
            skLineSegment(sketch, "E194.2", {"start": v(25.4, -169.83) * mm, "end": v(21.3, -167.47) * mm});
            skLineSegment(sketch, "E194.5", {"start": v(25.4, -160.37) * mm, "end": v(29.5, -162.73) * mm});
            skLineSegment(sketch, "E194.0", {"start": v(29.5, -162.73) * mm, "end": v(29.5, -167.47) * mm});
            skLineSegment(sketch, "E205", {"start": v(-25.4, -165.1) * mm, "end": v(-21.3, -165.1) * mm, "construction": true});
            skLineSegment(sketch, "E197.4", {"start": v(-29.5, -162.73) * mm, "end": v(-25.4, -160.37) * mm});
            skLineSegment(sketch, "E197.5", {"start": v(-25.4, -160.37) * mm, "end": v(-21.3, -162.73) * mm});
            skLineSegment(sketch, "E197.2", {"start": v(-25.4, -169.83) * mm, "end": v(-29.5, -167.47) * mm});
            skLineSegment(sketch, "E197.0", {"start": v(-21.3, -162.73) * mm, "end": v(-21.3, -167.47) * mm});
            skLineSegment(sketch, "E197.1", {"start": v(-21.3, -167.47) * mm, "end": v(-25.4, -169.83) * mm});
            skLineSegment(sketch, "E206", {"start": v(25.4, -114.3) * mm, "end": v(25.4, -165.1) * mm, "construction": true});
            skPoint(sketch, "E207", {"position": v(0, -211.15) * mm});
            skPoint(sketch, "E208.endSnap0", {"position": v(-36.6, -215.9) * mm});
            skLineSegment(sketch, "E209.1", {"start": v(29.5, -218.27) * mm, "end": v(25.4, -220.63) * mm});
            skPoint(sketch, "E210", {"position": v(0, -220.65) * mm});
            skLineSegment(sketch, "E211", {"start": v(0, -215.9) * mm, "end": v(25.4, -215.9) * mm, "construction": true});
            skLineSegment(sketch, "E208", {"start": v(0, -215.9) * mm, "end": v(-25.4, -215.9) * mm, "construction": true});
            skLineSegment(sketch, "E209.3", {"start": v(21.3, -218.27) * mm, "end": v(21.3, -213.53) * mm});
            skLineSegment(sketch, "E212.3", {"start": v(-29.5, -218.27) * mm, "end": v(-29.5, -213.53) * mm});
            skCircle(sketch, "E213", {"center": v(25.4, -215.9) * mm, "radius": 2.75 * mm});
            skLineSegment(sketch, "E214.0", {"start": v(-18.65, -211.15) * mm, "end": v(18.65, -211.15) * mm, "construction": true});
            skPoint(sketch, "E209.0.midPoint", {"position": v(29.5, -215.9) * mm});
            skPoint(sketch, "E212.0.midPoint", {"position": v(-21.3, -215.9) * mm});
            skPoint(sketch, "E215", {"position": v(0, -215.9) * mm});
            skCircle(sketch, "E216", {"center": v(-25.4, -215.9) * mm, "radius": 2.75 * mm});
            skPoint(sketch, "E211.endSnap0", {"position": v(36.6, -215.9) * mm});
            skLineSegment(sketch, "E217", {"start": v(25.4, -215.9) * mm, "end": v(29.5, -215.9) * mm, "construction": true});
            skLineSegment(sketch, "E209.4", {"start": v(21.3, -213.53) * mm, "end": v(25.4, -211.17) * mm});
            skCircle(sketch, "E209.cCircle", {"center": v(25.4, -215.9) * mm, "radius": 4.1 * mm, "construction": true});
            skCircle(sketch, "E212.cCircle", {"center": v(-25.4, -215.9) * mm, "radius": 4.1 * mm, "construction": true});
            skLineSegment(sketch, "E218", {"start": v(0, -211.15) * mm, "end": v(0, -220.65) * mm, "construction": true});
            skLineSegment(sketch, "E209.2", {"start": v(25.4, -220.63) * mm, "end": v(21.3, -218.27) * mm});
            skLineSegment(sketch, "E209.5", {"start": v(25.4, -211.17) * mm, "end": v(29.5, -213.53) * mm});
            skLineSegment(sketch, "E209.0", {"start": v(29.5, -213.53) * mm, "end": v(29.5, -218.27) * mm});
            skLineSegment(sketch, "E219", {"start": v(-25.4, -215.9) * mm, "end": v(-21.3, -215.9) * mm, "construction": true});
            skLineSegment(sketch, "E212.4", {"start": v(-29.5, -213.53) * mm, "end": v(-25.4, -211.17) * mm});
            skLineSegment(sketch, "E212.5", {"start": v(-25.4, -211.17) * mm, "end": v(-21.3, -213.53) * mm});
            skLineSegment(sketch, "E212.2", {"start": v(-25.4, -220.63) * mm, "end": v(-29.5, -218.27) * mm});
            skLineSegment(sketch, "E212.0", {"start": v(-21.3, -213.53) * mm, "end": v(-21.3, -218.27) * mm});
            skLineSegment(sketch, "E212.1", {"start": v(-21.3, -218.27) * mm, "end": v(-25.4, -220.63) * mm});
            skLineSegment(sketch, "E220", {"start": v(25.4, -165.1) * mm, "end": v(25.4, -215.9) * mm, "construction": true});
            skPoint(sketch, "E221", {"position": v(0, -58.75) * mm});
            skLineSegment(sketch, "E222.0", {"start": v(-18.65, -7.95) * mm, "end": v(18.65, -7.95) * mm, "construction": true});
            skPoint(sketch, "E223", {"position": v(0, -7.95) * mm});
            skLineSegment(sketch, "E224", {"start": v(0, -12.7) * mm, "end": v(-25.4, -12.7) * mm, "construction": true});
            skPoint(sketch, "E225.0.midPoint", {"position": v(-21.3, -12.7) * mm});
            skPoint(sketch, "E226.0.midPoint", {"position": v(29.5, -12.7) * mm});
            skPoint(sketch, "E227.endSnap0", {"position": v(75.79, -63.5) * mm});
            skPoint(sketch, "E228.endSnap0", {"position": v(75.79, -12.7) * mm});
            skPoint(sketch, "E229.0.midPoint", {"position": v(-21.3, -63.5) * mm});
            skCircle(sketch, "E230", {"center": v(25.4, -63.5) * mm, "radius": 2.75 * mm});
            skLineSegment(sketch, "E227", {"start": v(0, -63.5) * mm, "end": v(25.4, -63.5) * mm, "construction": true});
            skPoint(sketch, "E231", {"position": v(0, -12.7) * mm});
            skLineSegment(sketch, "E232.3", {"start": v(21.3, -65.87) * mm, "end": v(21.3, -61.13) * mm});
            skLineSegment(sketch, "E233.0", {"start": v(-18.65, -68.25) * mm, "end": v(18.65, -68.25) * mm, "construction": true});
            skPoint(sketch, "E234", {"position": v(0, -17.45) * mm});
            skLineSegment(sketch, "E225.1", {"start": v(-21.3, -15.07) * mm, "end": v(-25.4, -17.43) * mm});
            skPoint(sketch, "E232.0.midPoint", {"position": v(29.5, -63.5) * mm});
            skLineSegment(sketch, "E229.3", {"start": v(-29.5, -65.87) * mm, "end": v(-29.5, -61.13) * mm});
            skCircle(sketch, "E235", {"center": v(-25.4, -12.7) * mm, "radius": 2.75 * mm});
            skLineSegment(sketch, "E236.0", {"start": v(-18.65, -58.75) * mm, "end": v(18.65, -58.75) * mm, "construction": true});
            skLineSegment(sketch, "E226.3", {"start": v(21.3, -15.07) * mm, "end": v(21.3, -10.33) * mm});
            skLineSegment(sketch, "E237.0", {"start": v(-18.65, -17.45) * mm, "end": v(18.65, -17.45) * mm, "construction": true});
            skLineSegment(sketch, "E228", {"start": v(0, -12.7) * mm, "end": v(25.4, -12.7) * mm, "construction": true});
            skLineSegment(sketch, "E232.1", {"start": v(29.5, -65.87) * mm, "end": v(25.4, -68.23) * mm});
            skLineSegment(sketch, "E238", {"start": v(0, -63.5) * mm, "end": v(-25.4, -63.5) * mm, "construction": true});
            skLineSegment(sketch, "E225.3", {"start": v(-29.5, -15.07) * mm, "end": v(-29.5, -10.33) * mm});
            skPoint(sketch, "E238.endSnap0", {"position": v(-36.6, -63.5) * mm});
            skCircle(sketch, "E239", {"center": v(25.4, -12.7) * mm, "radius": 2.75 * mm});
            skLineSegment(sketch, "E240", {"start": v(25.4, -12.7) * mm, "end": v(25.4, -63.5) * mm, "construction": true});
            skCircle(sketch, "E241", {"center": v(-25.4, -63.5) * mm, "radius": 2.75 * mm});
            skPoint(sketch, "E242", {"position": v(0, -63.5) * mm});
            skPoint(sketch, "E224.endSnap0", {"position": v(-36.6, -12.7) * mm});
            skCircle(sketch, "E226.cCircle", {"center": v(25.4, -12.7) * mm, "radius": 4.1 * mm, "construction": true});
            skLineSegment(sketch, "E225.4", {"start": v(-29.5, -10.33) * mm, "end": v(-25.4, -7.97) * mm});
            skCircle(sketch, "E232.cCircle", {"center": v(25.4, -63.5) * mm, "radius": 4.1 * mm, "construction": true});
            skLineSegment(sketch, "E243", {"start": v(0, -58.75) * mm, "end": v(0, -68.25) * mm, "construction": true});
            skLineSegment(sketch, "E244", {"start": v(0, -7.95) * mm, "end": v(0, -17.45) * mm, "construction": true});
            skLineSegment(sketch, "E232.4", {"start": v(21.3, -61.13) * mm, "end": v(25.4, -58.77) * mm});
            skLineSegment(sketch, "E245.0.3", {"start": v(59.73, -5.92) * mm, "end": v(97.03, -5.92) * mm, "construction": true});
            skCircle(sketch, "E225.cCircle", {"center": v(-25.4, -12.7) * mm, "radius": 4.1 * mm, "construction": true});
            skCircle(sketch, "E229.cCircle", {"center": v(-25.4, -63.5) * mm, "radius": 4.1 * mm, "construction": true});
            skLineSegment(sketch, "E246", {"start": v(25.4, -63.5) * mm, "end": v(29.5, -63.5) * mm, "construction": true});
            skLineSegment(sketch, "E229.0", {"start": v(-21.3, -61.13) * mm, "end": v(-21.3, -65.87) * mm});
            skLineSegment(sketch, "E232.0", {"start": v(29.5, -61.13) * mm, "end": v(29.5, -65.87) * mm});
            skLineSegment(sketch, "E247", {"start": v(-25.4, -12.7) * mm, "end": v(-21.3, -12.7) * mm, "construction": true});
            skLineSegment(sketch, "E229.5", {"start": v(-25.4, -58.77) * mm, "end": v(-21.3, -61.13) * mm});
            skLineSegment(sketch, "E248", {"start": v(-25.4, -63.5) * mm, "end": v(-21.3, -63.5) * mm, "construction": true});
            skLineSegment(sketch, "E249", {"start": v(25.4, -12.7) * mm, "end": v(29.5, -12.7) * mm, "construction": true});
            skLineSegment(sketch, "E229.2", {"start": v(-25.4, -68.23) * mm, "end": v(-29.5, -65.87) * mm});
            skLineSegment(sketch, "E226.2", {"start": v(25.4, -17.43) * mm, "end": v(21.3, -15.07) * mm});
            skLineSegment(sketch, "E225.5", {"start": v(-25.4, -7.97) * mm, "end": v(-21.3, -10.33) * mm});
            skLineSegment(sketch, "E229.1", {"start": v(-21.3, -65.87) * mm, "end": v(-25.4, -68.23) * mm});
            skLineSegment(sketch, "E225.2", {"start": v(-25.4, -17.43) * mm, "end": v(-29.5, -15.07) * mm});
            skLineSegment(sketch, "E226.4", {"start": v(21.3, -10.33) * mm, "end": v(25.4, -7.97) * mm});
            skLineSegment(sketch, "E226.1", {"start": v(29.5, -15.07) * mm, "end": v(25.4, -17.43) * mm});
            skLineSegment(sketch, "E226.0", {"start": v(29.5, -10.33) * mm, "end": v(29.5, -15.07) * mm});
            skLineSegment(sketch, "E232.2", {"start": v(25.4, -68.23) * mm, "end": v(21.3, -65.87) * mm});
            skLineSegment(sketch, "E229.4", {"start": v(-29.5, -61.13) * mm, "end": v(-25.4, -58.77) * mm});
            skLineSegment(sketch, "E225.0", {"start": v(-21.3, -10.33) * mm, "end": v(-21.3, -15.07) * mm});
            skLineSegment(sketch, "E226.5", {"start": v(25.4, -7.97) * mm, "end": v(29.5, -10.33) * mm});
            skLineSegment(sketch, "E232.5", {"start": v(25.4, -58.77) * mm, "end": v(29.5, -61.13) * mm});
            skLineSegment(sketch, "E250", {"start": v(25.4, -114.3) * mm, "end": v(25.4, -63.5) * mm, "construction": true});
            skSolve(sketch);
        }
        {
            var Q0;
            Q0=makeQuery(id+"F4.imprint","IMPRINT",FACE,{"disambiguationData":[TD([[makeQuery(id+"F4.imprint","IMPRINT",EDGE,{"derivedFrom":sQuery(id+"F4.wireOp",EDGE,"E165.0.0")}),-1.0]])]});
            var Q1;
            Q1=makeQuery(id+"F4.imprint","IMPRINT",FACE,{"disambiguationData":[TD([[makeQuery(id+"F4.imprint","IMPRINT",EDGE,{"derivedFrom":sQuery(id+"F4.wireOp",EDGE,"E226.3")}),-1.0]])]});
            var Q2;
            Q2=makeQuery(id+"F4.imprint","IMPRINT",FACE,{"disambiguationData":[TD([[makeQuery(id+"F4.imprint","IMPRINT",EDGE,{"derivedFrom":sQuery(id+"F4.wireOp",EDGE,"E230")}),-1.0]])]});
            var Q3;
            Q3=makeQuery(id+"F4.imprint","IMPRINT",FACE,{"disambiguationData":[TD([[makeQuery(id+"F4.imprint","IMPRINT",EDGE,{"derivedFrom":sQuery(id+"F4.wireOp",EDGE,"E186.4")}),-1.0]])]});
            var Q4;
            Q4=makeQuery(id+"F4.imprint","IMPRINT",FACE,{"disambiguationData":[TD([[makeQuery(id+"F4.imprint","IMPRINT",EDGE,{"derivedFrom":sQuery(id+"F4.wireOp",EDGE,"E194.1")}),-1.0]])]});
            var Q5;
            Q5=makeQuery(id+"F4.imprint","IMPRINT",FACE,{"disambiguationData":[TD([[makeQuery(id+"F4.imprint","IMPRINT",EDGE,{"derivedFrom":sQuery(id+"F4.wireOp",EDGE,"E209.1")}),-1.0]])]});
            var Q6;
            Q6=makeQuery(id+"F4.imprint","IMPRINT",FACE,{"disambiguationData":[TD([[makeQuery(id+"F4.imprint","IMPRINT",EDGE,{"derivedFrom":sQuery(id+"F4.wireOp",EDGE,"E212.3")}),-1.0]])]});
            var Q7;
            Q7=makeQuery(id+"F4.imprint","IMPRINT",FACE,{"disambiguationData":[TD([[makeQuery(id+"F4.imprint","IMPRINT",EDGE,{"derivedFrom":sQuery(id+"F4.wireOp",EDGE,"E197.3")}),-1.0]])]});
            var Q8;
            Q8=makeQuery(id+"F4.imprint","IMPRINT",FACE,{"disambiguationData":[TD([[makeQuery(id+"F4.imprint","IMPRINT",EDGE,{"derivedFrom":sQuery(id+"F4.wireOp",EDGE,"E189.4")}),-1.0]])]});
            var Q9;
            Q9=makeQuery(id+"F4.imprint","IMPRINT",FACE,{"disambiguationData":[TD([[makeQuery(id+"F4.imprint","IMPRINT",EDGE,{"derivedFrom":sQuery(id+"F4.wireOp",EDGE,"E229.3")}),-1.0]])]});
            var Q10;
            Q10=makeQuery(id+"F4.imprint","IMPRINT",FACE,{"disambiguationData":[TD([[makeQuery(id+"F4.imprint","IMPRINT",EDGE,{"derivedFrom":sQuery(id+"F4.wireOp",EDGE,"E225.1")}),-1.0]])]});
            var Q11;
            Q11=makeQuery(id+"F4.imprint","IMPRINT",FACE,{"disambiguationData":[TD([[makeQuery(id+"F4.imprint","IMPRINT",EDGE,{"derivedFrom":sQuery(id+"F4.wireOp",EDGE,"E165.0.0")}),1.0]])]});
            extrude(context, id + "F5", {"entities" : qUnion([Q0, Q1, Q2, Q3, Q4, Q5, Q6, Q7, Q8, Q9, Q10, Q11]), "operationType" : NewBodyOperationType.ADD, "depth" : 5 * mm});
        }
        {
            var Q0;
            Q0=makeQuery(id+"F4.imprint","IMPRINT",FACE,{"disambiguationData":[TD([[makeQuery(id+"F4.imprint","IMPRINT",EDGE,{"derivedFrom":sQuery(id+"F4.wireOp",EDGE,"E226.3")}),-1.0]])]});
            var Q1;
            Q1=makeQuery(id+"F4.imprint","IMPRINT",FACE,{"disambiguationData":[TD([[makeQuery(id+"F4.imprint","IMPRINT",EDGE,{"derivedFrom":sQuery(id+"F4.wireOp",EDGE,"E225.1")}),-1.0]])]});
            var Q2;
            Q2=makeQuery(id+"F4.imprint","IMPRINT",FACE,{"disambiguationData":[TD([[makeQuery(id+"F4.imprint","IMPRINT",EDGE,{"derivedFrom":sQuery(id+"F4.wireOp",EDGE,"E229.3")}),-1.0]])]});
            var Q3;
            Q3=makeQuery(id+"F4.imprint","IMPRINT",FACE,{"disambiguationData":[TD([[makeQuery(id+"F4.imprint","IMPRINT",EDGE,{"derivedFrom":sQuery(id+"F4.wireOp",EDGE,"E189.4")}),-1.0]])]});
            var Q4;
            Q4=makeQuery(id+"F4.imprint","IMPRINT",FACE,{"disambiguationData":[TD([[makeQuery(id+"F4.imprint","IMPRINT",EDGE,{"derivedFrom":sQuery(id+"F4.wireOp",EDGE,"E197.3")}),-1.0]])]});
            var Q5;
            Q5=makeQuery(id+"F4.imprint","IMPRINT",FACE,{"disambiguationData":[TD([[makeQuery(id+"F4.imprint","IMPRINT",EDGE,{"derivedFrom":sQuery(id+"F4.wireOp",EDGE,"E212.3")}),-1.0]])]});
            var Q6;
            Q6=makeQuery(id+"F4.imprint","IMPRINT",FACE,{"disambiguationData":[TD([[makeQuery(id+"F4.imprint","IMPRINT",EDGE,{"derivedFrom":sQuery(id+"F4.wireOp",EDGE,"E209.1")}),-1.0]])]});
            var Q7;
            Q7=makeQuery(id+"F4.imprint","IMPRINT",FACE,{"disambiguationData":[TD([[makeQuery(id+"F4.imprint","IMPRINT",EDGE,{"derivedFrom":sQuery(id+"F4.wireOp",EDGE,"E194.1")}),-1.0]])]});
            var Q8;
            Q8=makeQuery(id+"F4.imprint","IMPRINT",FACE,{"disambiguationData":[TD([[makeQuery(id+"F4.imprint","IMPRINT",EDGE,{"derivedFrom":sQuery(id+"F4.wireOp",EDGE,"E186.4")}),-1.0]])]});
            var Q9;
            Q9=makeQuery(id+"F4.imprint","IMPRINT",FACE,{"disambiguationData":[TD([[makeQuery(id+"F4.imprint","IMPRINT",EDGE,{"derivedFrom":sQuery(id+"F4.wireOp",EDGE,"E230")}),-1.0]])]});
            extrude(context, id + "F6", {"entities" : qUnion([Q0, Q1, Q2, Q3, Q4, Q5, Q6, Q7, Q8, Q9]), "operationType" : NewBodyOperationType.REMOVE, "depth" : 4.5 * mm});
        }
    });
